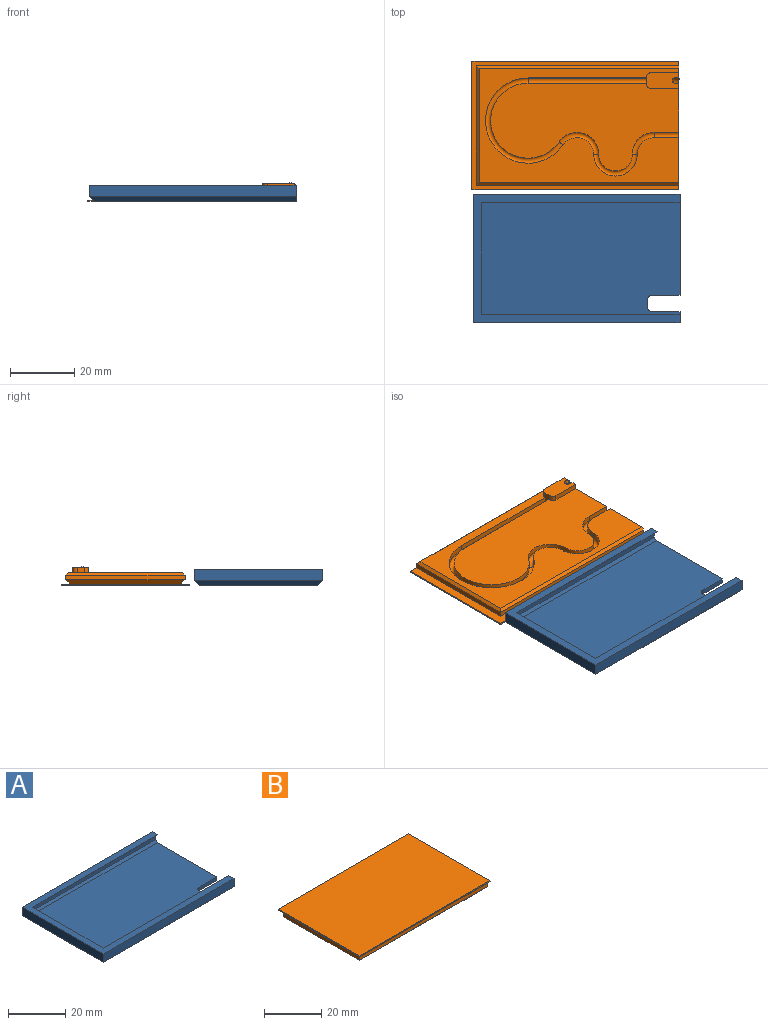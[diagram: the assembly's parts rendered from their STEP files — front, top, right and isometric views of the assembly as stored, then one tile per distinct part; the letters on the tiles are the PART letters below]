
ASSEMBLY  parts=2 mates=1
PART A: 25 faces, bbox 64.4x40x5.1 mm
  f0: plane 5.1x3.41mm, normal (1,0,0), area 9.7mm2, adj f1,f3,f4,f5,f6,f12,f16,f18
  f1: plane 62.82x36.8mm, normal (0,0,-1), area 2260.2mm2, adj f0,f2,f17,f18,f19,f20,f21,f22
  f2: plane 31.39x5.1mm, normal (1,0,0), area 51.6mm2, adj f1,f11,f12,f13,f14,f15,f16,f17
  f3: plane 64.42x3.5mm, normal (0,-1,0), area 225.5mm2, adj f0,f7,f12,f24
  f4: plane 63.12x0.86mm, normal (0,0.71,0.71), area 76.1mm2, adj f0,f5,f8,f16
  f5: plane 63.12x1.48mm, normal (0,1,0), area 93.6mm2, adj f0,f4,f6,f9
  f6: plane 63.12x1.26mm, normal (0,0.71,-0.71), area 111.2mm2, adj f0,f5,f10,f12
  f7: plane 40x3.5mm, normal (-1,0,0), area 140mm2, adj f3,f11,f12,f23
  f8: plane 37.4x0.86mm, normal (0.71,0,0.71), area 44.4mm2, adj f4,f9,f13,f16
  f9: plane 37.4x1.48mm, normal (1,0,0), area 55.5mm2, adj f5,f8,f10,f14
  f10: plane 37.4x1.26mm, normal (0.71,0,-0.71), area 64.3mm2, adj f6,f9,f12,f15
  f11: plane 64.42x3.5mm, normal (0,1,0), area 225.5mm2, adj f2,f7,f12,f22
  f12: plane 64.42x40mm, normal (0,0,1), area 418.9mm2, adj f0,f2,f3,f6,f7,f10,f11,f15
  f13: plane 63.12x0.86mm, normal (0,-0.71,0.71), area 76.1mm2, adj f2,f8,f14,f16
  f14: plane 63.12x1.48mm, normal (0,-1,0), area 93.6mm2, adj f2,f9,f13,f15
  f15: plane 63.12x1.26mm, normal (0,-0.71,-0.71), area 111.2mm2, adj f2,f10,f12,f14
  f16: plane 62.26x35.68mm, normal (0,0,1), area 2170.1mm2, adj f0,f2,f4,f8,f13,f17,f18,f19
  f17: plane 8.6x1.5mm, normal (0,-1,0), area 12.9mm2, adj f1,f2,f16,f21
  f18: plane 8.6x1.5mm, normal (0,1,0), area 12.9mm2, adj f0,f1,f16,f19
  f19: cylinder r=1.5mm len=1.5mm, axis (0,0,1), area 3.5mm2, adj f1,f16,f18,f20
  f20: plane 2.2x1.5mm, normal (1,0,0), area 3.3mm2, adj f1,f16,f19,f21
  f21: cylinder r=1.5mm len=1.5mm, axis (0,0,1), area 3.5mm2, adj f1,f16,f17,f20
  f22: plane 64.42x1.6mm, normal (0,0.71,-0.71), area 144mm2, adj f1,f2,f11,f23
  f23: plane 40x1.6mm, normal (-0.71,0,-0.71), area 86.9mm2, adj f1,f7,f22,f24
  f24: plane 64.42x1.6mm, normal (0,-0.71,-0.71), area 144mm2, adj f0,f1,f3,f23
PART B: 42 faces, bbox 66.2x41.4x7.9 mm
  f0: plane 58.62x27.39mm, normal (0,0,-1), area 1120.9mm2, adj f5,f7,f10,f13,f16,f19,f22,f25
  f1: plane 64.42x0.4mm, normal (0,-1,0), area 25.8mm2, adj f3,f5,f6,f32
  f2: plane 64.42x0.4mm, normal (0,1,0), area 25.8mm2, adj f3,f5,f6,f32
  f3: plane 40x0.4mm, normal (-1,0,0), area 16mm2, adj f1,f2,f6,f32
  f4: plane 62.22x35.6mm, normal (0,0,-1), area 824.8mm2, adj f5,f7,f8,f11,f14,f17,f20,f23
  f5: plane 41.23x6.83mm, normal (1,0,0), area 149.1mm2, adj f0,f1,f2,f4,f6,f23,f24,f25
  f6: plane 64.42x40mm, normal (0,0,1), area 2576.8mm2, adj f1,f2,f3,f5
  f7: plane 3.33x2.33mm, normal (-1,0,0), area 5.6mm2, adj f0,f4,f8,f10,f36,f39,f40,f41
  f8: plane 36.92x1.6mm, normal (0,1,0), area 59.1mm2, adj f4,f7,f9,f11
  f9: cylinder r=1mm len=36.92mm, axis (-1,0,0), area 164.8mm2, adj f8,f10,f12,f41
  f10: plane 36.92x1.6mm, normal (0,-1,0), area 59.1mm2, adj f0,f7,f9,f13
  f11: cylinder r=13.28mm len=26.55mm, axis (0,0,-1), area 87.3mm2, adj f4,f8,f12,f14
  f12: torus R=12.49mm, axis (0,0,-1), area 229mm2, adj f9,f11,f13,f15
  f13: cylinder r=11.7mm len=23.39mm, axis (0,0,-1), area 76.9mm2, adj f0,f10,f12,f16
  f14: cylinder r=5.22mm len=9.53mm, axis (0,0,1), area 21.2mm2, adj f4,f11,f15,f17
  f15: torus R=6.01mm, axis (0,0,1), area 68.1mm2, adj f12,f14,f16,f18
  f16: cylinder r=6.8mm len=12.41mm, axis (0,0,1), area 27.6mm2, adj f0,f13,f15,f19
  f17: cylinder r=6.78mm len=13.55mm, axis (0,0,-1), area 34.1mm2, adj f4,f14,f18,f20
  f18: torus R=5.99mm, axis (0,0,-1), area 83.9mm2, adj f15,f17,f19,f21
  f19: cylinder r=5.2mm len=10.39mm, axis (0,0,-1), area 26.1mm2, adj f0,f16,f18,f22
  f20: cylinder r=5.22mm len=5.22mm, axis (0,0,1), area 13.1mm2, adj f4,f17,f21,f23
  f21: torus R=6.01mm, axis (0,0,1), area 42.2mm2, adj f18,f20,f22,f24
  f22: cylinder r=6.8mm len=6.8mm, axis (0,0,1), area 17.1mm2, adj f0,f19,f21,f25
  f23: plane 7.69x1.6mm, normal (0,-1,0), area 12.3mm2, adj f4,f5,f20,f24
  f24: cylinder r=1mm len=7.69mm, axis (1,0,0), area 34.3mm2, adj f5,f21,f23,f25
  f25: plane 7.69x1.6mm, normal (0,1,0), area 12.3mm2, adj f0,f5,f22,f24
  f26: plane 63.02x0.8mm, normal (0,-0.71,-0.71), area 70.8mm2, adj f4,f5,f27,f29
  f27: plane 63.02x1.4mm, normal (0,-1,0), area 88.2mm2, adj f5,f26,f28,f30
  f28: plane 63.02x1.4mm, normal (0,-0.71,0.71), area 123.4mm2, adj f5,f27,f31,f32
  f29: plane 37.2x0.8mm, normal (-0.71,0,-0.71), area 41.2mm2, adj f4,f26,f30,f33
  f30: plane 37.2x1.4mm, normal (-1,0,0), area 52.1mm2, adj f27,f29,f31,f34
  f31: plane 37.2x1.4mm, normal (-0.71,0,0.71), area 70.9mm2, adj f28,f30,f32,f35
  f32: plane 64.42x40mm, normal (0,0,-1), area 457.1mm2, adj f1,f2,f3,f5,f28,f31,f35
  f33: plane 63.02x0.8mm, normal (0,0.71,-0.71), area 70.8mm2, adj f4,f5,f29,f34
  f34: plane 63.02x1.4mm, normal (0,1,0), area 88.2mm2, adj f5,f30,f33,f35
  f35: plane 63.02x1.4mm, normal (0,0.71,0.71), area 123.4mm2, adj f5,f31,f32,f34
  f36: plane 11.38x6.38mm, normal (0,0,-1), area 45.8mm2, adj f5,f7,f37,f38,f39,f40,f41
  f37: plane 8.6x1.6mm, normal (0,1,0), area 13.8mm2, adj f0,f5,f36,f40
  f38: plane 8.6x1.6mm, normal (0,-1,0), area 13.8mm2, adj f4,f5,f36,f39
  f39: cylinder r=1.4mm len=1.6mm, axis (0,0,1), area 3.5mm2, adj f4,f7,f36,f38
  f40: cylinder r=1.4mm len=1.6mm, axis (0,0,1), area 3.5mm2, adj f0,f7,f36,f37
  f41: bspline ~10.39x5.74mm, area 66.5mm2, adj f5,f7,f9,f36
PLACE A at identity fixed
PLACE B rot(axis=(1,0,0),180deg) t=(-0.4,81.49,-5.6)mm
MATE planar B.f6 <-> A.f1  axis (0,0,-1) through (-32.61,61.49,-5.6)mm
